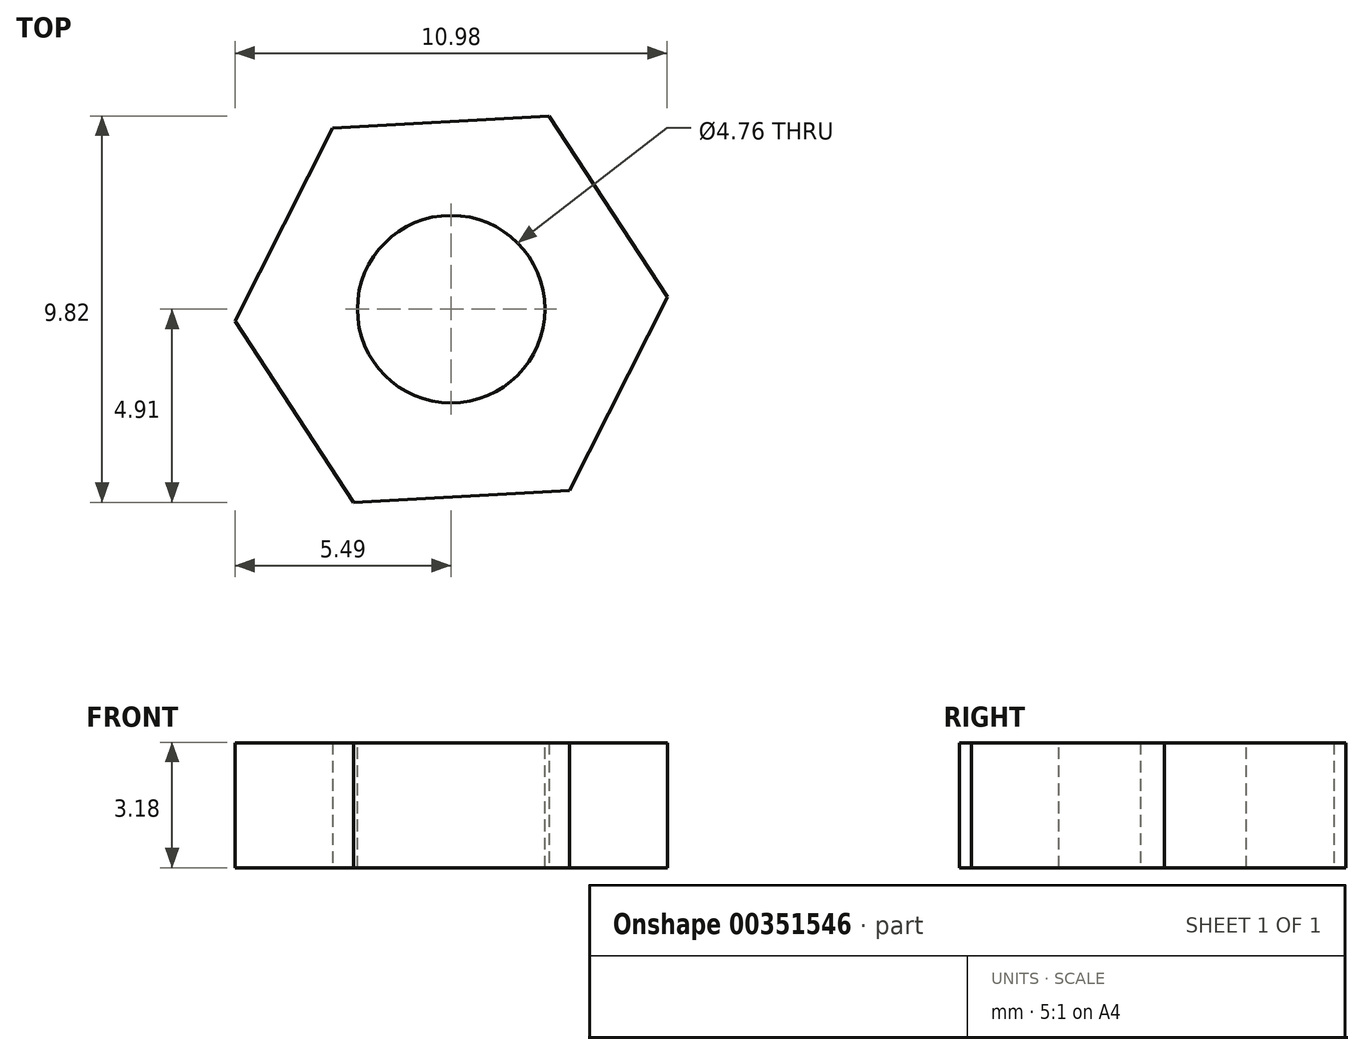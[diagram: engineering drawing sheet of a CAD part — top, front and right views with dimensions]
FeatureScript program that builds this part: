
annotation { "Feature Type Name" : "Feature", "Feature Type Description" : "" }
export const myFeature = defineFeature(function(context is Context, id is Id, definition is map)
    precondition{}
    {
        {
            var Q0;
            Q0=qCreatedBy(makeId("Top.planeOp"),FACE);
            var sketch = newSketch(context, id + "F0", { "sketchPlane" : qUnion([Q0])});
            skCircle(sketch, "E0.cCircle", {"center": v(0, 0) * mm, "radius": 4.76 * mm, "construction": true});
            skLineSegment(sketch, "E0.0", {"start": v(2.48, 4.9) * mm, "end": v(5.5, 0.3) * mm});
            skLineSegment(sketch, "E0.1", {"start": v(5.5, 0.3) * mm, "end": v(3, -4.6) * mm});
            skLineSegment(sketch, "E0.2", {"start": v(3, -4.6) * mm, "end": v(-2.48, -4.9) * mm});
            skLineSegment(sketch, "E0.3", {"start": v(-2.48, -4.9) * mm, "end": v(-5.5, -0.3) * mm});
            skLineSegment(sketch, "E0.4", {"start": v(-5.5, -0.3) * mm, "end": v(-3, 4.6) * mm});
            skLineSegment(sketch, "E0.5", {"start": v(-3, 4.6) * mm, "end": v(2.48, 4.9) * mm});
            skPoint(sketch, "E0.0.midPoint", {"position": v(3.99, 2.6) * mm});
            skSolve(sketch);
        }
        {
            var Q0;
            Q0 = qSketchRegion(id + "F0", true);
            extrude(context, id + "F1", {"entities" : qUnion([Q0]), "depth" : 3.17 * mm});
        }
        {
            var Q0;
            Q0=makeQuery(id+"F1.opExtrude","CAP_FACE",FACE,{"disambiguationData":[OSD([sQuery(id+"F0.wireOp",EDGE,"E0.0"),sQuery(id+"F0.wireOp",EDGE,"E0.1"),sQuery(id+"F0.wireOp",EDGE,"E0.2"),sQuery(id+"F0.wireOp",EDGE,"E0.3"),sQuery(id+"F0.wireOp",EDGE,"E0.4"),sQuery(id+"F0.wireOp",EDGE,"E0.5")])],"isStart":false});
            var sketch = newSketch(context, id + "F2", { "sketchPlane" : qUnion([Q0])});
            skCircle(sketch, "E1", {"center": v(0, 0) * mm, "radius": 2.38 * mm});
            skSolve(sketch);
        }
        {
            var Q0;
            Q0 = qSketchRegion(id + "F2", true);
            extrude(context, id + "F3", {"entities" : qUnion([Q0]), "operationType" : NewBodyOperationType.REMOVE, "endBound" : BoundingType.THROUGH_ALL, "oppositeDirection" : true, "depth" : 25.4 * mm});
        }
    });
